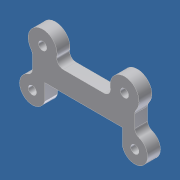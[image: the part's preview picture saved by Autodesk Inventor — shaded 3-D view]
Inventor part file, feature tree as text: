
AUTODESK INVENTOR PART (.ipt)
format: ipt  version: unknown  size: 222,208 bytes
history: native  units: in
note: dims shown in document units (in); Inventor stores cm internally (conversion verified against a paired STEP export)
features: fillet x6, extrude x1, sketch x1
ambient origin geometry x8: Origin, YZ Plane, XZ Plane, XY Plane, X Axis, Y Axis, Z Axis, Center Point
bodies: Solid1 (feature_tree)
feature tree (8):
  extrude  "Extrusion1"  Depth=0.4693in
  fillet  "Fillet1"  Radius=0.16in
  fillet  "Fillet2"  Radius=0.4in
  fillet  "Fillet3"  Radius=2.0in
  fillet  "Fillet4"  Radius=1.52in
  fillet  "Fillet5"  Radius=0.25in
  fillet  "Fillet6"  Radius=0.125in
  sketch  "Sketch1"  dims[d27=0.24in d28=0.4693in d29=0.16in d30=0.4in d31=2.0in d32=1.52in d33=0.25in d34=0.0in d35=0.125in d36=0.125in d37=0.125in d38=0.125in d39=0.125in d40=0.125in]
